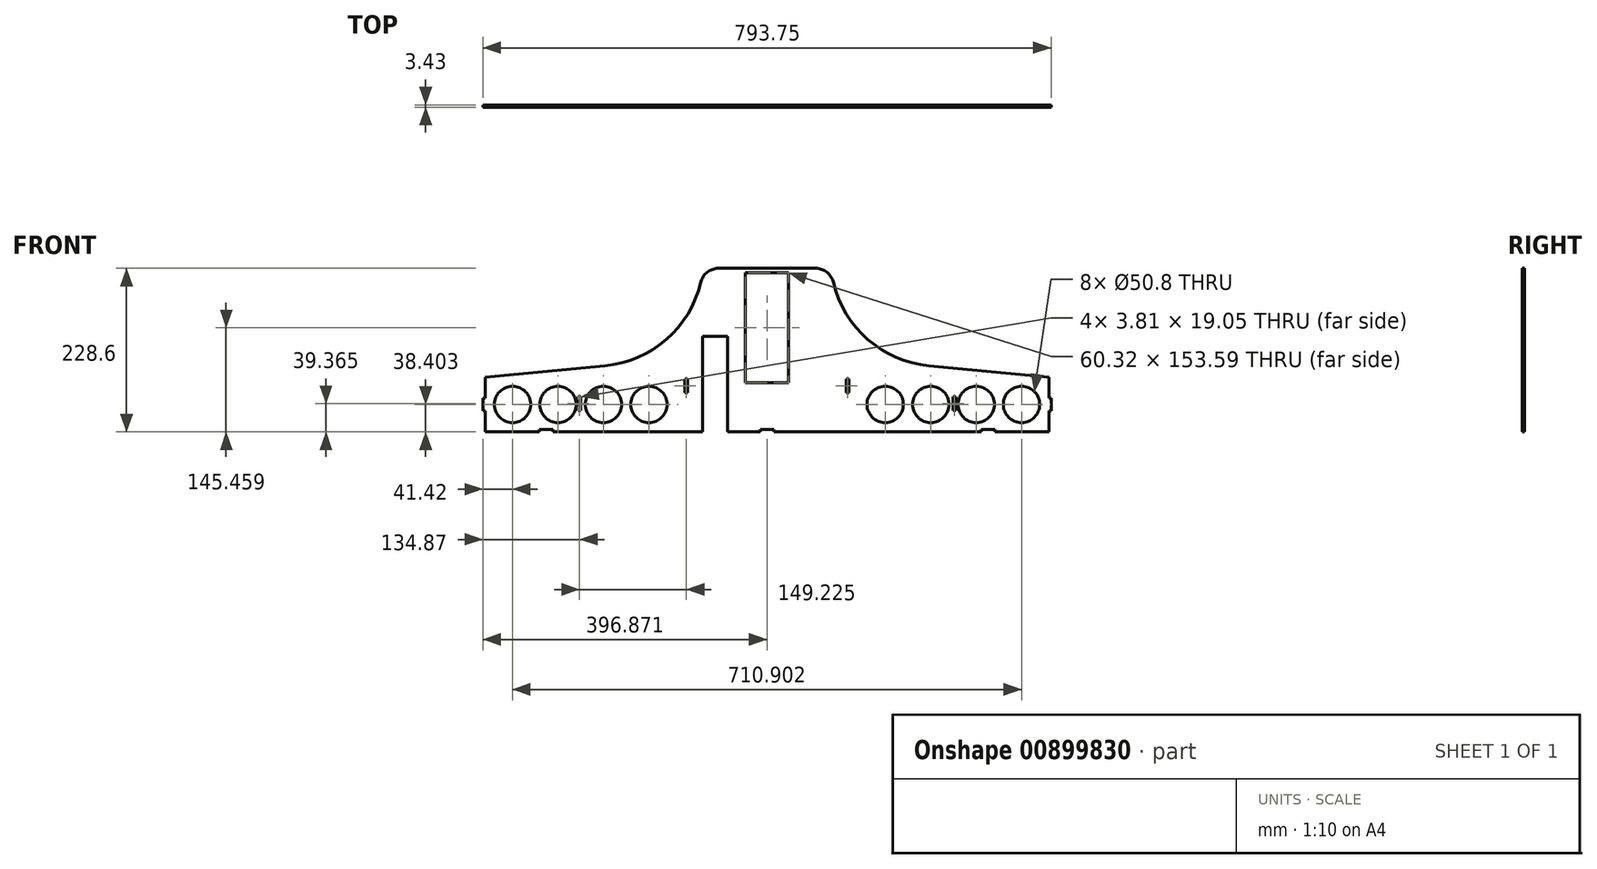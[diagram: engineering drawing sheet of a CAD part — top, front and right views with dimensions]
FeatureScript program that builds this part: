
annotation { "Feature Type Name" : "Feature", "Feature Type Description" : "" }
export const myFeature = defineFeature(function(context is Context, id is Id, definition is map)
    precondition{}
    {
        {
            var Q0;
            Q0=qCreatedBy(makeId("Front.planeOp"),FACE);
            var sketch = newSketch(context, id + "F0", { "sketchPlane" : qUnion([Q0])});
            skLineSegment(sketch, "E0", {"start": v(431.8, -24.06) * mm, "end": v(492.12, -24.06) * mm});
            skLineSegment(sketch, "E1", {"start": v(431.8, -177.66) * mm, "end": v(431.8, -24.06) * mm});
            skLineSegment(sketch, "E2", {"start": v(492.12, -177.66) * mm, "end": v(431.8, -177.66) * mm});
            skLineSegment(sketch, "E3", {"start": v(492.12, -24.06) * mm, "end": v(492.12, -177.66) * mm});
            skLineSegment(sketch, "E4", {"start": v(68.26, -246.32) * mm, "end": v(143.83, -246.32) * mm});
            skLineSegment(sketch, "E5", {"start": v(68.26, -217.11) * mm, "end": v(68.26, -246.32) * mm});
            skLineSegment(sketch, "E6", {"start": v(65.09, -217.11) * mm, "end": v(68.26, -217.11) * mm});
            skLineSegment(sketch, "E7", {"start": v(65.09, -199.33) * mm, "end": v(65.09, -217.11) * mm});
            skLineSegment(sketch, "E8", {"start": v(68.26, -199.33) * mm, "end": v(65.09, -199.33) * mm});
            skLineSegment(sketch, "E9", {"start": v(68.26, -170.12) * mm, "end": v(68.26, -199.33) * mm});
            skLineSegment(sketch, "E10", {"start": v(68.26, -170.12) * mm, "end": v(235.7, -153.94) * mm});
            skArc(sketch, "E11", {"start": v(235.7, -153.94) * mm, "mid": v(321.25, -117.06) * mm, "end": v(369.36, -37.29) * mm});
            skArc(sketch, "E12", {"start": v(394.08, -17.72) * mm, "mid": v(378.32, -23.2) * mm, "end": v(369.36, -37.29) * mm});
            skLineSegment(sketch, "E13", {"start": v(394.08, -17.72) * mm, "end": v(529.85, -17.72) * mm});
            skArc(sketch, "E14", {"start": v(554.57, -37.29) * mm, "mid": v(545.6, -23.2) * mm, "end": v(529.85, -17.72) * mm});
            skArc(sketch, "E15", {"start": v(554.57, -37.29) * mm, "mid": v(602.67, -117.06) * mm, "end": v(688.22, -153.94) * mm});
            skLineSegment(sketch, "E16", {"start": v(688.22, -153.94) * mm, "end": v(855.66, -170.12) * mm});
            skLineSegment(sketch, "E17", {"start": v(855.66, -170.12) * mm, "end": v(855.66, -199.33) * mm});
            skLineSegment(sketch, "E18", {"start": v(858.84, -199.33) * mm, "end": v(855.66, -199.33) * mm});
            skLineSegment(sketch, "E19", {"start": v(858.84, -217.11) * mm, "end": v(858.84, -199.33) * mm});
            skLineSegment(sketch, "E20", {"start": v(855.66, -217.11) * mm, "end": v(858.84, -217.11) * mm});
            skLineSegment(sketch, "E21", {"start": v(855.66, -217.11) * mm, "end": v(855.66, -246.32) * mm});
            skLineSegment(sketch, "E22", {"start": v(780.1, -246.32) * mm, "end": v(855.66, -246.32) * mm});
            skLineSegment(sketch, "E23", {"start": v(780.1, -246.32) * mm, "end": v(780.1, -243.15) * mm});
            skLineSegment(sketch, "E24", {"start": v(780.1, -243.15) * mm, "end": v(761.05, -243.15) * mm});
            skLineSegment(sketch, "E25", {"start": v(761.05, -243.15) * mm, "end": v(761.05, -246.32) * mm});
            skLineSegment(sketch, "E26", {"start": v(471.49, -246.32) * mm, "end": v(761.05, -246.32) * mm});
            skLineSegment(sketch, "E27", {"start": v(471.49, -246.32) * mm, "end": v(471.49, -243.15) * mm});
            skLineSegment(sketch, "E28", {"start": v(471.49, -243.15) * mm, "end": v(452.44, -243.15) * mm});
            skLineSegment(sketch, "E29", {"start": v(452.44, -243.15) * mm, "end": v(452.44, -246.32) * mm});
            skLineSegment(sketch, "E30", {"start": v(406.72, -246.32) * mm, "end": v(452.44, -246.32) * mm});
            skLineSegment(sketch, "E31", {"start": v(406.72, -246.32) * mm, "end": v(406.72, -112.97) * mm});
            skLineSegment(sketch, "E32", {"start": v(406.72, -112.97) * mm, "end": v(371.8, -112.97) * mm});
            skLineSegment(sketch, "E33", {"start": v(371.8, -112.97) * mm, "end": v(371.8, -246.32) * mm});
            skLineSegment(sketch, "E34", {"start": v(162.88, -246.32) * mm, "end": v(371.8, -246.32) * mm});
            skLineSegment(sketch, "E35", {"start": v(162.88, -246.32) * mm, "end": v(162.88, -243.15) * mm});
            skLineSegment(sketch, "E36", {"start": v(162.88, -243.15) * mm, "end": v(143.83, -243.15) * mm});
            skLineSegment(sketch, "E37", {"start": v(143.83, -243.15) * mm, "end": v(143.83, -246.32) * mm});
            skLineSegment(sketch, "E38", {"start": v(572.83, -191.71) * mm, "end": v(576.64, -191.71) * mm});
            skLineSegment(sketch, "E39", {"start": v(576.64, -191.71) * mm, "end": v(576.64, -172.66) * mm});
            skLineSegment(sketch, "E40", {"start": v(576.64, -172.66) * mm, "end": v(572.83, -172.66) * mm});
            skLineSegment(sketch, "E41", {"start": v(572.83, -172.66) * mm, "end": v(572.83, -191.71) * mm});
            skLineSegment(sketch, "E42", {"start": v(722.06, -216.48) * mm, "end": v(725.87, -216.48) * mm});
            skLineSegment(sketch, "E43", {"start": v(725.87, -216.48) * mm, "end": v(725.87, -197.43) * mm});
            skLineSegment(sketch, "E44", {"start": v(725.87, -197.43) * mm, "end": v(722.06, -197.43) * mm});
            skLineSegment(sketch, "E45", {"start": v(722.06, -197.43) * mm, "end": v(722.06, -216.48) * mm});
            skLineSegment(sketch, "E46", {"start": v(201.87, -216.48) * mm, "end": v(201.87, -197.43) * mm});
            skLineSegment(sketch, "E47", {"start": v(201.87, -197.43) * mm, "end": v(198.06, -197.43) * mm});
            skLineSegment(sketch, "E48", {"start": v(198.06, -197.43) * mm, "end": v(198.06, -216.48) * mm});
            skLineSegment(sketch, "E49", {"start": v(198.06, -216.48) * mm, "end": v(201.87, -216.48) * mm});
            skLineSegment(sketch, "E50", {"start": v(351.1, -191.71) * mm, "end": v(351.1, -172.66) * mm});
            skLineSegment(sketch, "E51", {"start": v(351.1, -172.66) * mm, "end": v(347.28, -172.66) * mm});
            skLineSegment(sketch, "E52", {"start": v(347.28, -172.66) * mm, "end": v(347.28, -191.71) * mm});
            skLineSegment(sketch, "E53", {"start": v(347.28, -191.71) * mm, "end": v(351.1, -191.71) * mm});
            skCircle(sketch, "E54", {"center": v(106.51, -207.92) * mm, "radius": 25.4 * mm});
            skCircle(sketch, "E55", {"center": v(169.86, -207.92) * mm, "radius": 25.4 * mm});
            skCircle(sketch, "E56", {"center": v(233.36, -207.92) * mm, "radius": 25.4 * mm});
            skCircle(sketch, "E57", {"center": v(296.96, -207.92) * mm, "radius": 25.4 * mm});
            skCircle(sketch, "E58", {"center": v(626.97, -207.92) * mm, "radius": 25.4 * mm});
            skCircle(sketch, "E59", {"center": v(690.56, -207.92) * mm, "radius": 25.4 * mm});
            skCircle(sketch, "E60", {"center": v(754.06, -207.92) * mm, "radius": 25.4 * mm});
            skCircle(sketch, "E61", {"center": v(817.41, -207.92) * mm, "radius": 25.4 * mm});
            skSolve(sketch);
        }
        {
            var Q0;
            Q0 = qSketchRegion(id + "F0", true);
            extrude(context, id + "F1", {"entities" : qUnion([Q0]), "depth" : 3.43 * mm, "offsetDistance" : 25.4 * mm});
        }
    });
